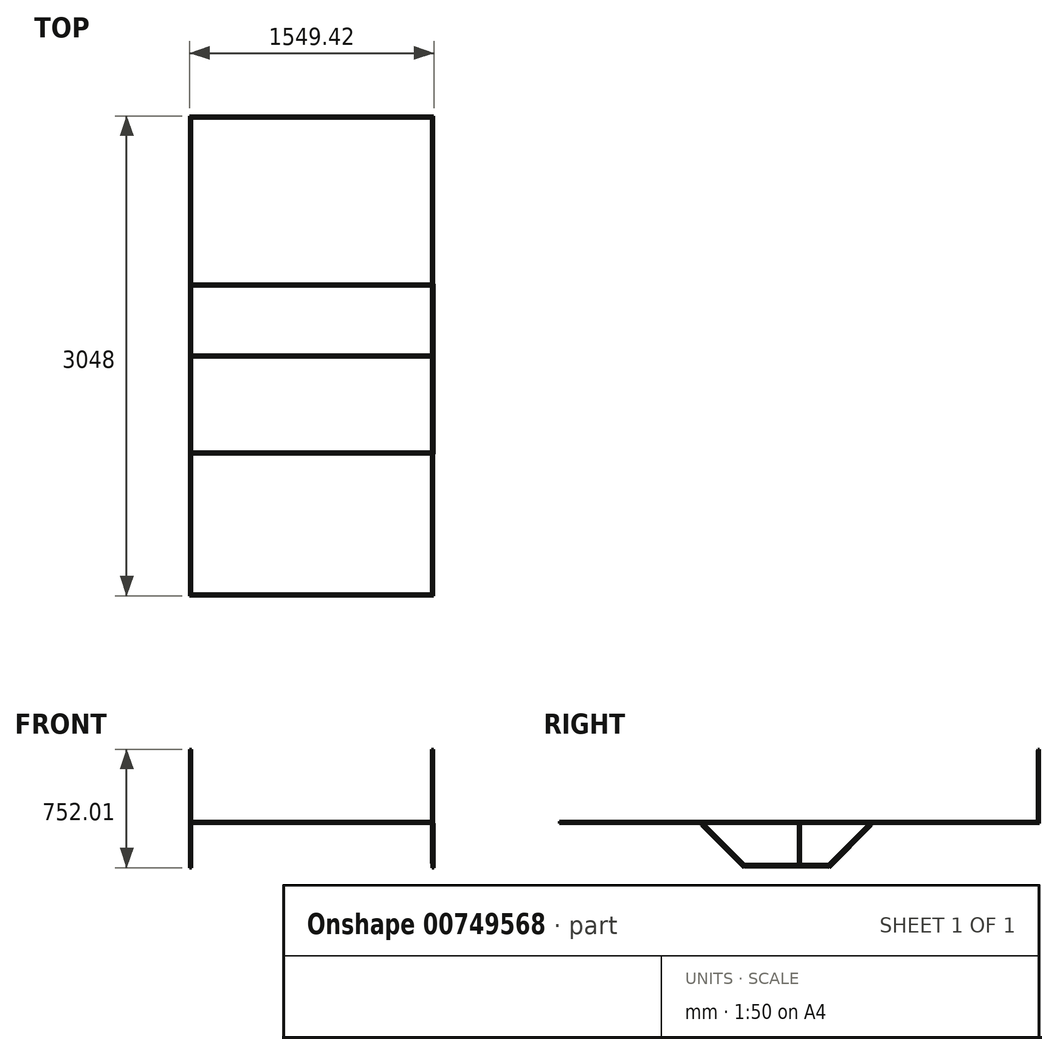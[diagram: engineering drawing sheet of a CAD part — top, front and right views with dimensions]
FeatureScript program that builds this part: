
annotation { "Feature Type Name" : "Feature", "Feature Type Description" : "" }
export const myFeature = defineFeature(function(context is Context, id is Id, definition is map)
    precondition{}
    {
        {
            var Q0;
            Q0=qCreatedBy(makeId("Front.planeOp"),FACE);
            var sketch = newSketch(context, id + "F0", { "sketchPlane" : qUnion([Q0])});
            skLineSegment(sketch, "E0", {"start": v(-49.7, 0) * mm, "end": v(1474.3, 0) * mm});
            skLineSegment(sketch, "E1.bottom", {"start": v(-49.7, 0) * mm, "end": v(-62.4, 0) * mm});
            skLineSegment(sketch, "E1.top", {"start": v(-49.7, -12.7) * mm, "end": v(-62.4, -12.7) * mm});
            skLineSegment(sketch, "E1.left", {"start": v(-49.7, 0) * mm, "end": v(-49.7, -12.7) * mm});
            skLineSegment(sketch, "E1.right", {"start": v(-62.4, 0) * mm, "end": v(-62.4, -12.7) * mm});
            skLineSegment(sketch, "E2.bottom", {"start": v(1474.3, 0) * mm, "end": v(1487, 0) * mm});
            skLineSegment(sketch, "E2.top", {"start": v(1474.3, -12.7) * mm, "end": v(1487, -12.7) * mm});
            skLineSegment(sketch, "E2.left", {"start": v(1474.3, 0) * mm, "end": v(1474.3, -12.7) * mm});
            skLineSegment(sketch, "E2.right", {"start": v(1487, 0) * mm, "end": v(1487, -12.7) * mm});
            skSolve(sketch);
        }
        {
            var Q0;
            Q0 = qSketchRegion(id + "F0", true);
            extrude(context, id + "F1", {"entities" : qUnion([Q0]), "depth" : 3048 * mm, "offsetDistance" : 25.4 * mm});
        }
        {
            var Q0;
            Q0=makeQuery(id+"F1.opExtrude","SWEPT_FACE",FACE,{"disambiguationData":[OSD([sQuery(id+"F0.wireOp",EDGE,"E2.left")])]});
            var sketch = newSketch(context, id + "F2", { "sketchPlane" : qUnion([Q0])});
            skLineSegment(sketch, "E3.bottom", {"start": v(0, 0) * mm, "end": v(12.7, 0) * mm});
            skLineSegment(sketch, "E3.top", {"start": v(0, -12.7) * mm, "end": v(12.7, -12.7) * mm});
            skLineSegment(sketch, "E3.left", {"start": v(0, 0) * mm, "end": v(0, -12.7) * mm});
            skLineSegment(sketch, "E3.right", {"start": v(12.7, 0) * mm, "end": v(12.7, -12.7) * mm});
            skLineSegment(sketch, "E4.bottom", {"start": v(3048, -12.7) * mm, "end": v(3035.3, -12.7) * mm});
            skLineSegment(sketch, "E4.top", {"start": v(3048, 0) * mm, "end": v(3035.3, 0) * mm});
            skLineSegment(sketch, "E4.left", {"start": v(3048, -12.7) * mm, "end": v(3048, 0) * mm});
            skLineSegment(sketch, "E4.right", {"start": v(3035.3, -12.7) * mm, "end": v(3035.3, 0) * mm});
            skSolve(sketch);
        }
        {
            var Q0;
            Q0 = qSketchRegion(id + "F2", true);
            extrude(context, id + "F3", {"entities" : qUnion([Q0]), "depth" : 1524 * mm, "offsetDistance" : 25.4 * mm});
        }
        {
            var Q0;
            Q0=makeQuery(id+"F1.opExtrude","SWEPT_FACE",FACE,{"disambiguationData":[OSD([sQuery(id+"F0.wireOp",EDGE,"E2.right")])]});
            var sketch = newSketch(context, id + "F4", { "sketchPlane" : qUnion([Q0])});
            skLineSegment(sketch, "E5", {"start": v(-3048, -12.7) * mm, "end": v(-1524, -12.7) * mm});
            skLineSegment(sketch, "E6.bottom", {"start": v(-1517.65, -12.72) * mm, "end": v(-1530.35, -12.72) * mm});
            skLineSegment(sketch, "E6.top", {"start": v(-1517.65, -0.02) * mm, "end": v(-1530.35, -0.02) * mm});
            skLineSegment(sketch, "E6.left", {"start": v(-1517.65, -12.72) * mm, "end": v(-1517.65, -0.02) * mm});
            skLineSegment(sketch, "E6.right", {"start": v(-1530.35, -12.72) * mm, "end": v(-1530.35, -0.02) * mm});
            skPoint(sketch, "E6.middle", {"position": v(-1524, -6.37) * mm});
            skSolve(sketch);
        }
        {
            var Q0;
            {var subQ1=sQuery(id+"F4.wireOp",EDGE,"E6.top");Q0=makeQuery(id+"F4.imprint","IMPRINT",FACE,{"disambiguationData":[TD([[makeQuery(id+"F4.imprint","IMPRINT",EDGE,{"derivedFrom":subQ1}),1.0]])]});}
            extrude(context, id + "F5", {"entities" : qUnion([Q0]), "oppositeDirection" : true, "depth" : 1539.24 * mm, "offsetDistance" : 25.4 * mm});
        }
        {
            var Q0;
            Q0=makeQuery(id+"F1.opExtrude","SWEPT_FACE",FACE,{"disambiguationData":[OSD([sQuery(id+"F0.wireOp",EDGE,"E2.top")])]});
            var sketch = newSketch(context, id + "F6", { "sketchPlane" : qUnion([Q0])});
            skLineSegment(sketch, "E7.bottom", {"start": v(1487, 1530.35) * mm, "end": v(1474.3, 1530.35) * mm});
            skLineSegment(sketch, "E7.top", {"start": v(1487, 1517.65) * mm, "end": v(1474.3, 1517.65) * mm});
            skLineSegment(sketch, "E7.left", {"start": v(1487, 1530.35) * mm, "end": v(1487, 1517.65) * mm});
            skLineSegment(sketch, "E7.right", {"start": v(1474.3, 1530.35) * mm, "end": v(1474.3, 1517.65) * mm});
            skLineSegment(sketch, "E8.bottom", {"start": v(-49.7, 1517.65) * mm, "end": v(-62.4, 1517.65) * mm});
            skLineSegment(sketch, "E8.top", {"start": v(-49.7, 1530.35) * mm, "end": v(-62.4, 1530.35) * mm});
            skLineSegment(sketch, "E8.left", {"start": v(-49.7, 1517.65) * mm, "end": v(-49.7, 1530.35) * mm});
            skLineSegment(sketch, "E8.right", {"start": v(-62.4, 1517.65) * mm, "end": v(-62.4, 1530.35) * mm});
            skSolve(sketch);
        }
        {
            var Q0;
            Q0 = qSketchRegion(id + "F6", true);
            extrude(context, id + "F7", {"entities" : qUnion([Q0]), "depth" : 254 * mm, "offsetDistance" : 25.4 * mm});
        }
        {
            var Q0;
            Q0=makeQuery(id+"F1.opExtrude","SWEPT_FACE",FACE,{"disambiguationData":[OSD([sQuery(id+"F0.wireOp",EDGE,"E2.right")])]});
            var sketch = newSketch(context, id + "F8", { "sketchPlane" : qUnion([Q0])});
            skLineSegment(sketch, "E9", {"start": v(-3048, 0) * mm, "end": v(-2133.6, 0) * mm});
            skLineSegment(sketch, "E10.bottom", {"start": v(-2133.6, 0) * mm, "end": v(-2146.3, 0) * mm});
            skLineSegment(sketch, "E10.top", {"start": v(-2133.6, -12.7) * mm, "end": v(-2146.3, -12.7) * mm});
            skLineSegment(sketch, "E10.left", {"start": v(-2133.6, 0) * mm, "end": v(-2133.6, -12.7) * mm});
            skLineSegment(sketch, "E10.right", {"start": v(-2146.3, 0) * mm, "end": v(-2146.3, -12.7) * mm});
            skSolve(sketch);
        }
        {
            var Q0;
            Q0 = qSketchRegion(id + "F8", true);
            extrude(context, id + "F9", {"entities" : qUnion([Q0]), "oppositeDirection" : true, "depth" : 1549.4 * mm, "offsetDistance" : 25.4 * mm});
        }
        {
            var Q0;
            Q0=makeQuery(id+"F1.opExtrude","SWEPT_FACE",FACE,{"disambiguationData":[OSD([sQuery(id+"F0.wireOp",EDGE,"E1.right")])]});
            var sketch = newSketch(context, id + "F10", { "sketchPlane" : qUnion([Q0])});
            skLineSegment(sketch, "E11", {"start": v(0, 0) * mm, "end": v(1066.8, 0) * mm});
            skLineSegment(sketch, "E12.bottom", {"start": v(1066.8, 0) * mm, "end": v(1079.5, 0) * mm});
            skLineSegment(sketch, "E12.top", {"start": v(1066.8, -12.7) * mm, "end": v(1079.5, -12.7) * mm});
            skLineSegment(sketch, "E12.left", {"start": v(1066.8, 0) * mm, "end": v(1066.8, -12.7) * mm});
            skLineSegment(sketch, "E12.right", {"start": v(1079.5, 0) * mm, "end": v(1079.5, -12.7) * mm});
            skSolve(sketch);
        }
        {
            var Q0;
            Q0=makeQuery(id+"F10.imprint","IMPRINT",FACE,{"disambiguationData":[TD([[makeQuery(id+"F10.imprint","IMPRINT",EDGE,{"derivedFrom":sQuery(id+"F10.wireOp",EDGE,"E12.bottom")}),1.0]])]});
            extrude(context, id + "F11", {"entities" : qUnion([Q0]), "oppositeDirection" : true, "depth" : 1549.4 * mm, "offsetDistance" : 25.4 * mm});
        }
        {
            var Q0;
            Q0=makeQuery(id+"F1.opExtrude","SWEPT_FACE",FACE,{"disambiguationData":[OSD([sQuery(id+"F0.wireOp",EDGE,"E1.top")])]});
            var sketch = newSketch(context, id + "F12", { "sketchPlane" : qUnion([Q0])});
            skLineSegment(sketch, "E13.bottom", {"start": v(-62.4, 2146.32) * mm, "end": v(-49.7, 2146.32) * mm});
            skLineSegment(sketch, "E13.top", {"start": v(-62.4, 2133.63) * mm, "end": v(-49.7, 2133.63) * mm});
            skLineSegment(sketch, "E13.left", {"start": v(-62.4, 2146.32) * mm, "end": v(-62.4, 2133.63) * mm});
            skLineSegment(sketch, "E13.right", {"start": v(-49.7, 2146.32) * mm, "end": v(-49.7, 2133.63) * mm});
            skLineSegment(sketch, "E14.bottom", {"start": v(1487.02, 2146.32) * mm, "end": v(1474.32, 2146.32) * mm});
            skLineSegment(sketch, "E14.top", {"start": v(1487.02, 2133.63) * mm, "end": v(1474.32, 2133.63) * mm});
            skLineSegment(sketch, "E14.left", {"start": v(1487.02, 2146.32) * mm, "end": v(1487.02, 2133.63) * mm});
            skLineSegment(sketch, "E14.right", {"start": v(1474.32, 2146.32) * mm, "end": v(1474.32, 2133.63) * mm});
            skLineSegment(sketch, "E15.bottom", {"start": v(1474.32, 1079.34) * mm, "end": v(1487.02, 1079.34) * mm});
            skLineSegment(sketch, "E15.top", {"start": v(1474.32, 1066.64) * mm, "end": v(1487.02, 1066.64) * mm});
            skLineSegment(sketch, "E15.left", {"start": v(1474.32, 1079.34) * mm, "end": v(1474.32, 1066.64) * mm});
            skLineSegment(sketch, "E15.right", {"start": v(1487.02, 1079.34) * mm, "end": v(1487.02, 1066.64) * mm});
            skLineSegment(sketch, "E16.bottom", {"start": v(-49.7, 1079.4) * mm, "end": v(-62.4, 1079.4) * mm});
            skLineSegment(sketch, "E16.top", {"start": v(-49.7, 1066.7) * mm, "end": v(-62.4, 1066.7) * mm});
            skLineSegment(sketch, "E16.left", {"start": v(-49.7, 1079.4) * mm, "end": v(-49.7, 1066.7) * mm});
            skLineSegment(sketch, "E16.right", {"start": v(-62.4, 1079.4) * mm, "end": v(-62.4, 1066.7) * mm});
            skSolve(sketch);
        }
        {
            var Q0;
            Q0 = qSketchRegion(id + "F12", true);
            extrude(context, id + "F13", {"entities" : qUnion([Q0]), "depth" : 12.7 * mm, "offsetDistance" : 25.4 * mm});
        }
        {
            var Q0;
            Q0=makeQuery(id+"F13.opExtrude","CAP_EDGE",EDGE,{"disambiguationData":[OSD([sQuery(id+"F12.wireOp",EDGE,"E13.top")])],"isStart":false});
            var Q1;
            Q1=makeQuery(id+"F13.opExtrude","CAP_EDGE",EDGE,{"disambiguationData":[OSD([sQuery(id+"F12.wireOp",EDGE,"E14.top")])],"isStart":false});
            chamfer(context, id + "F14", {"entities" : qUnion([Q0, Q1]), "chamferType" : ChamferType.TWO_OFFSETS, "width1" : 12.7 * mm, "oppositeDirection" : false, "width2" : 12.7 * mm, "tangentPropagation" : true});
        }
        {
            var Q0;
            Q0=makeQuery(id+"F13.opExtrude","CAP_EDGE",EDGE,{"disambiguationData":[OSD([sQuery(id+"F12.wireOp",EDGE,"E15.bottom")])],"isStart":false});
            var Q1;
            Q1=makeQuery(id+"F13.opExtrude","CAP_EDGE",EDGE,{"disambiguationData":[OSD([sQuery(id+"F12.wireOp",EDGE,"E16.bottom")])],"isStart":false});
            chamfer(context, id + "F15", {"entities" : qUnion([Q0, Q1]), "chamferType" : ChamferType.TWO_OFFSETS, "width1" : 12.7 * mm, "oppositeDirection" : false, "width2" : 12.7 * mm, "tangentPropagation" : true});
        }
        {
            var Q0;
            Q0=makeQuery(id+"F15.opChamfer","BLEND_FACE",FACE,{"disambiguationData":[OSD([sQuery(id+"F12.wireOp",EDGE,"E15.bottom")])]});
            var Q1;
            Q1=makeQuery(id+"F15.opChamfer","BLEND_FACE",FACE,{"disambiguationData":[OSD([sQuery(id+"F12.wireOp",EDGE,"E16.bottom")])]});
            extrude(context, id + "F16", {"entities" : qUnion([Q0, Q1]), "depth" : 381 * mm, "offsetDistance" : 25.4 * mm});
        }
        {
            var Q0;
            Q0=makeQuery(id+"F16.opExtrude","CAP_EDGE",EDGE,{"disambiguationData":[OSD([sQuery(id+"F12.wireOp",EDGE,"E15.bottom"),sQuery(id+"F12.wireOp",EDGE,"E15.top"),sQuery(id+"F12.wireOp",EDGE,"E15.left"),sQuery(id+"F12.wireOp",EDGE,"E15.right")])],"isStart":false});
            var Q1;
            Q1=makeQuery(id+"F16.opExtrude","CAP_EDGE",EDGE,{"disambiguationData":[OSD([sQuery(id+"F12.wireOp",EDGE,"E16.bottom"),sQuery(id+"F12.wireOp",EDGE,"E16.top"),sQuery(id+"F12.wireOp",EDGE,"E16.left"),sQuery(id+"F12.wireOp",EDGE,"E16.right")])],"isStart":false});
            chamfer(context, id + "F17", {"entities" : qUnion([Q0, Q1]), "chamferType" : ChamferType.TWO_OFFSETS, "width1" : 12.7 * mm, "oppositeDirection" : false, "width2" : 12.7 * mm, "tangentPropagation" : true});
        }
        {
            var Q0;
            Q0=makeQuery(id+"F17.opChamfer","BLEND_FACE",FACE,{"disambiguationData":[OSD([sQuery(id+"F12.wireOp",EDGE,"E16.bottom"),sQuery(id+"F12.wireOp",EDGE,"E16.top"),sQuery(id+"F12.wireOp",EDGE,"E16.left"),sQuery(id+"F12.wireOp",EDGE,"E16.right")])]});
            var Q1;
            Q1=makeQuery(id+"F17.opChamfer","BLEND_FACE",FACE,{"disambiguationData":[OSD([sQuery(id+"F12.wireOp",EDGE,"E15.bottom"),sQuery(id+"F12.wireOp",EDGE,"E15.top"),sQuery(id+"F12.wireOp",EDGE,"E15.left"),sQuery(id+"F12.wireOp",EDGE,"E15.right")])]});
            extrude(context, id + "F18", {"entities" : qUnion([Q0, Q1]), "depth" : 482.6 * mm, "offsetDistance" : 25.4 * mm});
        }
        {
            var Q0;
            Q0=makeQuery(id+"F14.opChamfer","BLEND_FACE",FACE,{"disambiguationData":[OSD([sQuery(id+"F12.wireOp",EDGE,"E13.top")])]});
            var Q1;
            Q1=makeQuery(id+"F14.opChamfer","BLEND_FACE",FACE,{"disambiguationData":[OSD([sQuery(id+"F12.wireOp",EDGE,"E14.top")])]});
            extrude(context, id + "F19", {"entities" : qUnion([Q0, Q1]), "depth" : 381 * mm, "offsetDistance" : 25.4 * mm});
        }
        {
            var Q0;
            Q0=makeQuery(id+"F19.opExtrude","CAP_EDGE",EDGE,{"disambiguationData":[OSD([sQuery(id+"F12.wireOp",EDGE,"E13.bottom"),sQuery(id+"F12.wireOp",EDGE,"E13.top"),sQuery(id+"F12.wireOp",EDGE,"E13.left"),sQuery(id+"F12.wireOp",EDGE,"E13.right")])],"isStart":false});
            var Q1;
            Q1=makeQuery(id+"F19.opExtrude","CAP_EDGE",EDGE,{"disambiguationData":[OSD([sQuery(id+"F12.wireOp",EDGE,"E14.bottom"),sQuery(id+"F12.wireOp",EDGE,"E14.top"),sQuery(id+"F12.wireOp",EDGE,"E14.left"),sQuery(id+"F12.wireOp",EDGE,"E14.right")])],"isStart":false});
            chamfer(context, id + "F20", {"entities" : qUnion([Q0, Q1]), "chamferType" : ChamferType.TWO_OFFSETS, "width1" : 12.7 * mm, "oppositeDirection" : false, "width2" : 12.7 * mm, "tangentPropagation" : true});
        }
        {
            var Q0;
            Q0=makeQuery(id+"F20.opChamfer","BLEND_FACE",FACE,{"disambiguationData":[OSD([sQuery(id+"F12.wireOp",EDGE,"E13.bottom"),sQuery(id+"F12.wireOp",EDGE,"E13.top"),sQuery(id+"F12.wireOp",EDGE,"E13.left"),sQuery(id+"F12.wireOp",EDGE,"E13.right")])]});
            var Q1;
            Q1=makeQuery(id+"F20.opChamfer","BLEND_FACE",FACE,{"disambiguationData":[OSD([sQuery(id+"F12.wireOp",EDGE,"E14.bottom"),sQuery(id+"F12.wireOp",EDGE,"E14.top"),sQuery(id+"F12.wireOp",EDGE,"E14.left"),sQuery(id+"F12.wireOp",EDGE,"E14.right")])]});
            extrude(context, id + "F21", {"entities" : qUnion([Q0, Q1]), "depth" : 127 * mm, "offsetDistance" : 25.4 * mm});
        }
        {
            var Q0;
            Q0=makeQuery(id+"F1.opExtrude","SWEPT_FACE",FACE,{"disambiguationData":[OSD([sQuery(id+"F0.wireOp",EDGE,"E1.bottom")])]});
            var sketch = newSketch(context, id + "F22", { "sketchPlane" : qUnion([Q0])});
            skLineSegment(sketch, "E17.bottom", {"start": v(-62.4, 0) * mm, "end": v(-49.7, 0) * mm});
            skLineSegment(sketch, "E17.top", {"start": v(-62.4, -12.7) * mm, "end": v(-49.7, -12.7) * mm});
            skLineSegment(sketch, "E17.left", {"start": v(-62.4, 0) * mm, "end": v(-62.4, -12.7) * mm});
            skLineSegment(sketch, "E17.right", {"start": v(-49.7, 0) * mm, "end": v(-49.7, -12.7) * mm});
            skLineSegment(sketch, "E18.bottom", {"start": v(1487, 0) * mm, "end": v(1474.3, 0) * mm});
            skLineSegment(sketch, "E18.top", {"start": v(1487, -12.7) * mm, "end": v(1474.3, -12.7) * mm});
            skLineSegment(sketch, "E18.left", {"start": v(1487, 0) * mm, "end": v(1487, -12.7) * mm});
            skLineSegment(sketch, "E18.right", {"start": v(1474.3, 0) * mm, "end": v(1474.3, -12.7) * mm});
            skSolve(sketch);
        }
        {
            var Q0;
            Q0 = qSketchRegion(id + "F22", true);
            extrude(context, id + "F23", {"entities" : qUnion([Q0]), "depth" : 457.2 * mm, "offsetDistance" : 25.4 * mm});
        }
        {
            var Q0;
            Q0=makeQuery(id+"F23.opExtrude","CAP_EDGE",EDGE,{"disambiguationData":[OSD([sQuery(id+"F22.wireOp",EDGE,"E18.top")])],"isStart":false});
            chamfer(context, id + "F24", {"entities" : qUnion([Q0]), "chamferType" : ChamferType.OFFSET_ANGLE, "width" : 12.7 * mm, "oppositeDirection" : false, "angle" : 10 * degree, "tangentPropagation" : true});
        }
        {
            var Q0;
            Q0=makeQuery(id+"F23.opExtrude","CAP_EDGE",EDGE,{"disambiguationData":[OSD([sQuery(id+"F22.wireOp",EDGE,"E17.top")])],"isStart":false});
            chamfer(context, id + "F25", {"entities" : qUnion([Q0]), "chamferType" : ChamferType.TWO_OFFSETS, "width1" : 2.3 * mm, "oppositeDirection" : false, "width2" : 12.7 * mm, "tangentPropagation" : true});
        }
    });
